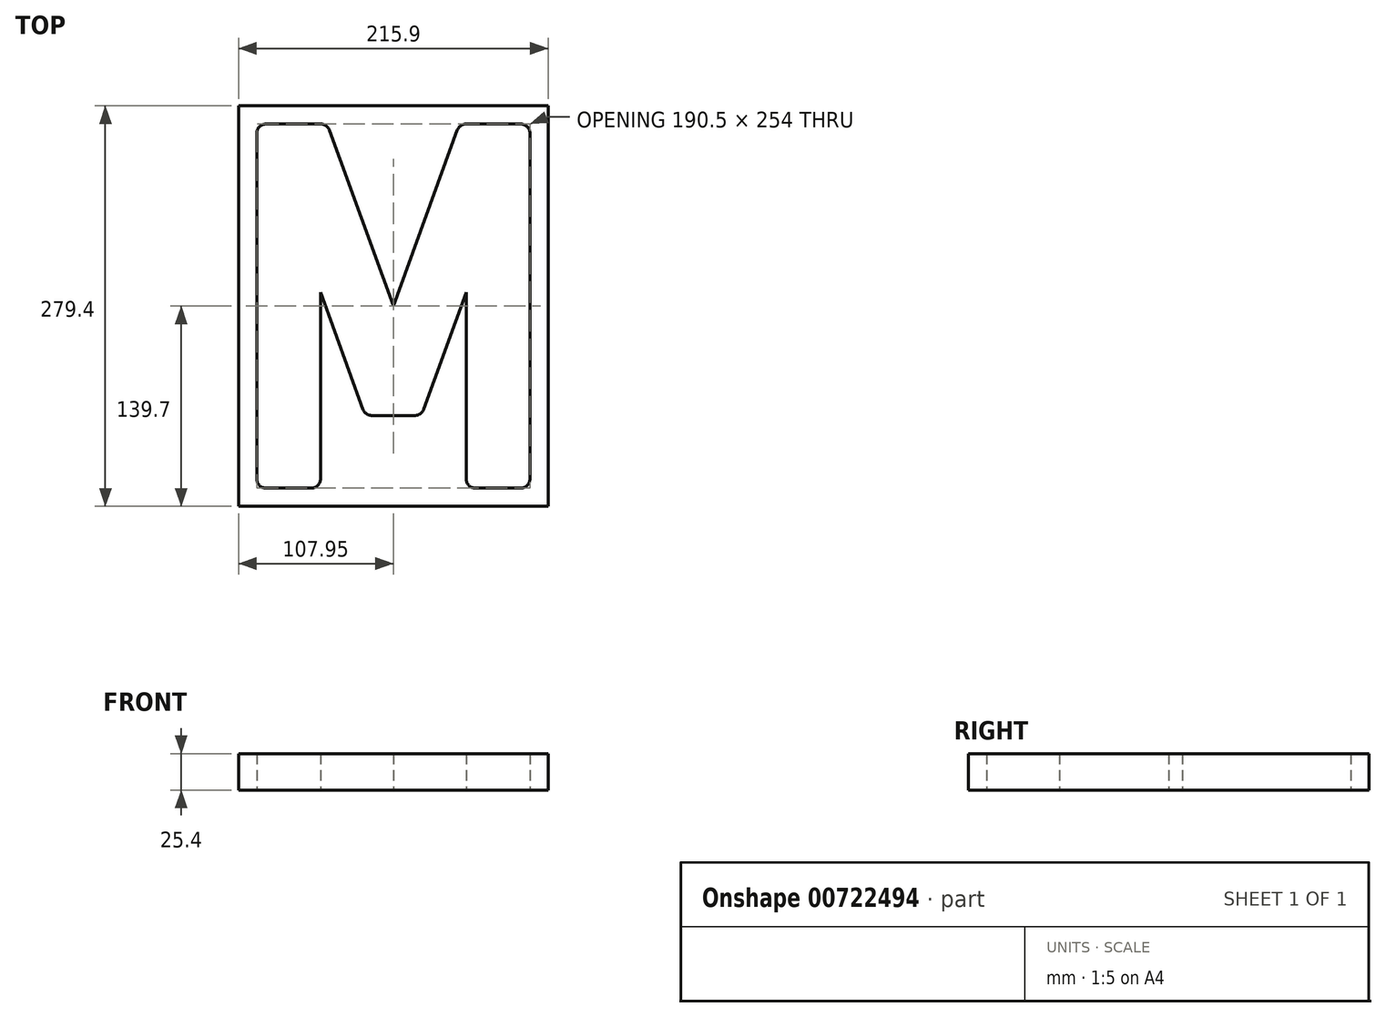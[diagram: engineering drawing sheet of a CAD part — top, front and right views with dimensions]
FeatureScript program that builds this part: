
annotation { "Feature Type Name" : "Feature", "Feature Type Description" : "" }
export const myFeature = defineFeature(function(context is Context, id is Id, definition is map)
    precondition{}
    {
        {
            var Q0;
            Q0=qCreatedBy(makeId("Top.planeOp"),FACE);
            var sketch = newSketch(context, id + "F0", { "sketchPlane" : qUnion([Q0])});
            skLineSegment(sketch, "E0.bottom", {"start": v(-107.95, 139.7) * mm, "end": v(107.95, 139.7) * mm});
            skLineSegment(sketch, "E0.top", {"start": v(-107.95, -139.7) * mm, "end": v(107.95, -139.7) * mm});
            skLineSegment(sketch, "E0.left", {"start": v(-107.95, 139.7) * mm, "end": v(-107.95, -139.7) * mm});
            skLineSegment(sketch, "E0.right", {"start": v(107.95, 139.7) * mm, "end": v(107.95, -139.7) * mm});
            skLineSegment(sketch, "E1", {"start": v(0, 139.7) * mm, "end": v(0, -139.7) * mm, "construction": true});
            skLineSegment(sketch, "E2", {"start": v(-107.95, 0) * mm, "end": v(107.95, 0) * mm, "construction": true});
            skLineSegment(sketch, "E3", {"start": v(-95.25, 120.65) * mm, "end": v(-95.25, -120.65) * mm});
            skLineSegment(sketch, "E4", {"start": v(-88.9, -127) * mm, "end": v(-57.15, -127) * mm});
            skLineSegment(sketch, "E5", {"start": v(-50.8, -120.65) * mm, "end": v(-50.8, 9.6) * mm});
            skLineSegment(sketch, "E6", {"start": v(-50.8, 9.6) * mm, "end": v(-21.03, -72.17) * mm});
            skLineSegment(sketch, "E7", {"start": v(0, 0) * mm, "end": v(-44.7, 122.82) * mm});
            skLineSegment(sketch, "E8", {"start": v(-50.67, 127) * mm, "end": v(-88.9, 127) * mm});
            skLineSegment(sketch, "E9", {"start": v(-15.07, -76.35) * mm, "end": v(0, -76.35) * mm});
            skPoint(sketch, "E10.visualSharp", {"position": v(-95.25, 127) * mm});
            skArc(sketch, "E10.filletArc", {"start": v(-88.9, 127) * mm, "mid": v(-93.4, 125.14) * mm, "end": v(-95.25, 120.65) * mm});
            skPoint(sketch, "E11.visualSharp", {"position": v(-46.22, 127) * mm});
            skArc(sketch, "E11.filletArc", {"start": v(-44.7, 122.82) * mm, "mid": v(-47.03, 125.85) * mm, "end": v(-50.67, 127) * mm});
            skPoint(sketch, "E12.visualSharp", {"position": v(-95.25, -127) * mm});
            skArc(sketch, "E12.filletArc", {"start": v(-95.25, -120.65) * mm, "mid": v(-93.4, -125.14) * mm, "end": v(-88.9, -127) * mm});
            skPoint(sketch, "E13.visualSharp", {"position": v(-50.8, -127) * mm});
            skArc(sketch, "E13.filletArc", {"start": v(-57.15, -127) * mm, "mid": v(-52.66, -125.14) * mm, "end": v(-50.8, -120.65) * mm});
            skPoint(sketch, "E14.visualSharp", {"position": v(-19.51, -76.35) * mm});
            skArc(sketch, "E14.filletArc", {"start": v(-21.03, -72.17) * mm, "mid": v(-18.7, -75.2) * mm, "end": v(-15.07, -76.35) * mm});
            skLineSegment(sketch, "E15.MirrorCS", {"start": v(0, 0) * mm, "end": v(44.7, 122.82) * mm});
            skLineSegment(sketch, "E16.MirrorCS", {"start": v(50.67, 127) * mm, "end": v(88.9, 127) * mm});
            skLineSegment(sketch, "E17.MirrorCS", {"start": v(95.25, 120.65) * mm, "end": v(95.25, -120.65) * mm});
            skLineSegment(sketch, "E18.MirrorCS", {"start": v(50.8, 9.6) * mm, "end": v(21.03, -72.17) * mm});
            skLineSegment(sketch, "E19.MirrorCS", {"start": v(50.8, -120.65) * mm, "end": v(50.8, 9.6) * mm});
            skLineSegment(sketch, "E20.MirrorCS", {"start": v(88.9, -127) * mm, "end": v(57.15, -127) * mm});
            skArc(sketch, "E21.MirrorCS", {"start": v(21.03, -72.17) * mm, "mid": v(18.7, -75.2) * mm, "end": v(15.07, -76.35) * mm});
            skLineSegment(sketch, "E22.MirrorCS", {"start": v(15.07, -76.35) * mm, "end": v(0, -76.35) * mm});
            skArc(sketch, "E23.MirrorCS", {"start": v(57.15, -127) * mm, "mid": v(52.66, -125.14) * mm, "end": v(50.8, -120.65) * mm});
            skArc(sketch, "E24.MirrorCS", {"start": v(95.25, -120.65) * mm, "mid": v(93.4, -125.14) * mm, "end": v(88.9, -127) * mm});
            skArc(sketch, "E25.MirrorCS", {"start": v(44.7, 122.82) * mm, "mid": v(47.03, 125.85) * mm, "end": v(50.67, 127) * mm});
            skArc(sketch, "E26.MirrorCS", {"start": v(88.9, 127) * mm, "mid": v(93.4, 125.14) * mm, "end": v(95.25, 120.65) * mm});
            skSolve(sketch);
        }
        {
            var Q0;
            Q0=makeQuery(id+"F0.imprint","IMPRINT",FACE,{"disambiguationData":[TD([[makeQuery(id+"F0.imprint","IMPRINT",EDGE,{"derivedFrom":sQuery(id+"F0.wireOp",EDGE,"E0.bottom")}),-1.0]])]});
            extrude(context, id + "F1", {"entities" : qUnion([Q0]), "depth" : 25.4 * mm, "offsetDistance" : 25.4 * mm});
        }
    });
